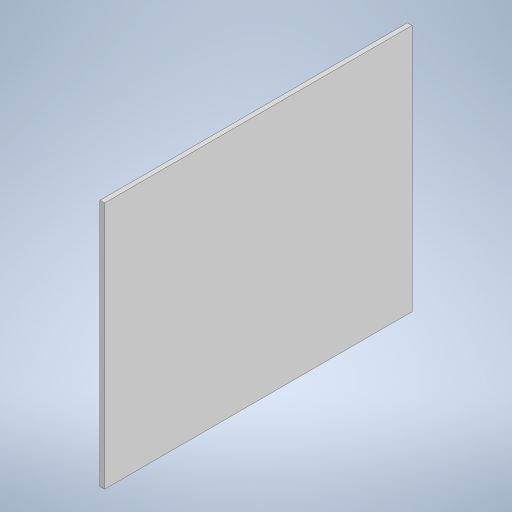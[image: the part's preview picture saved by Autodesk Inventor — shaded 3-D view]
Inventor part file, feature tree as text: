
AUTODESK INVENTOR PART (.ipt)
format: ipt  version: 2024.3 (Build 283343000, 343)  size: 190,464 bytes
history: native  units: mm
features: extrude x1, sketch x1
ambient origin geometry x8: Origin, YZ Plane, XZ Plane, XY Plane, X Axis, Y Axis, Z Axis, Center Point
bodies: Solid1 (feature_tree)
feature tree (2):
  extrude  "Extrusion1"  Depth=161.261mm
  sketch  "Sketch1"  dims[d0=200.0mm d1=161.261mm d2=3.0mm d3=0.0mm]
